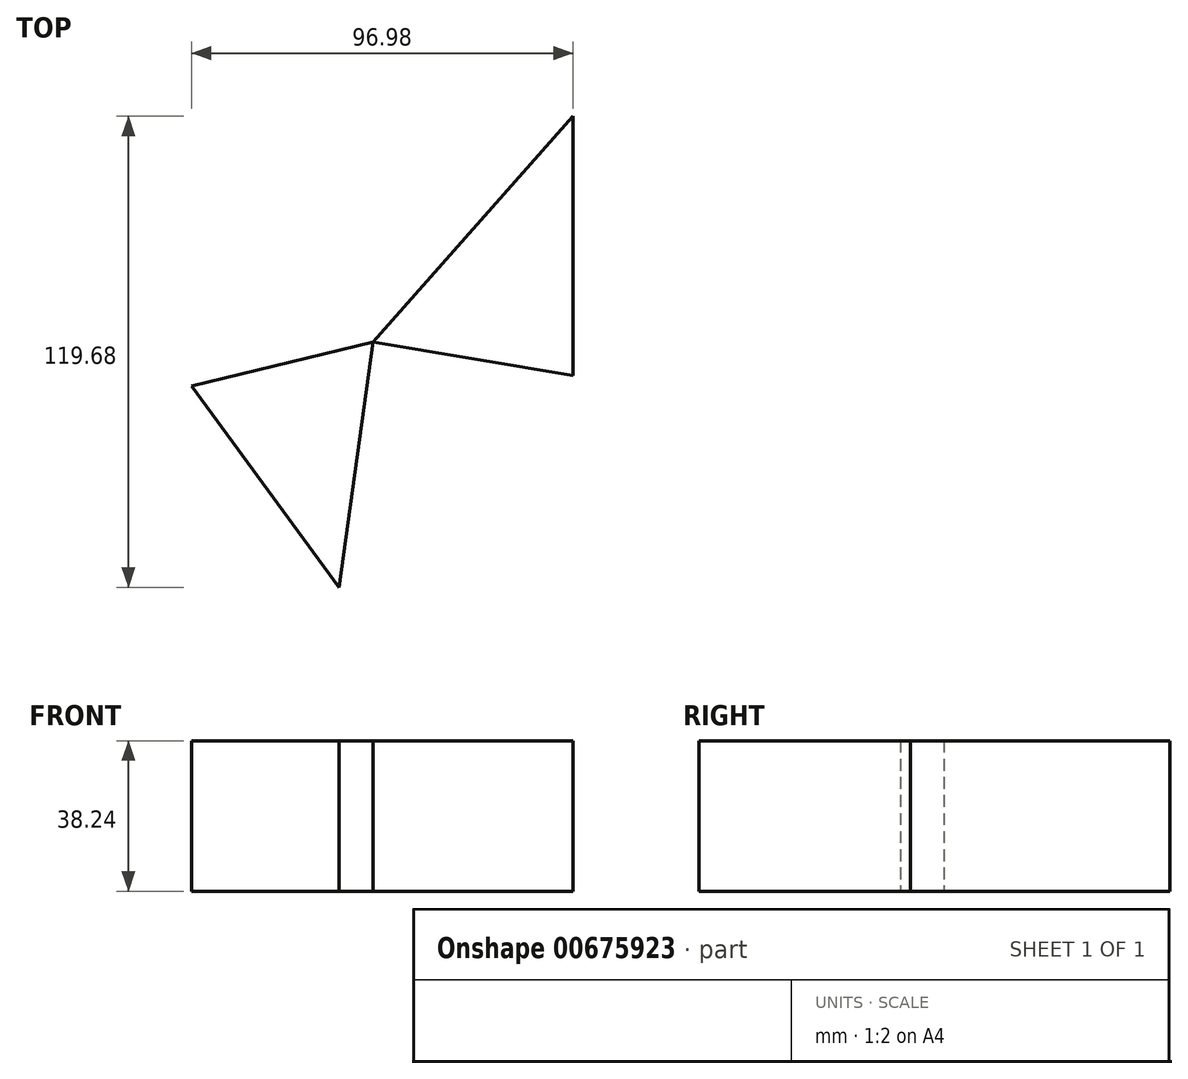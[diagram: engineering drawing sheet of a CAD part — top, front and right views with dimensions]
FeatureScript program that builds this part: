
annotation { "Feature Type Name" : "Feature", "Feature Type Description" : "" }
export const myFeature = defineFeature(function(context is Context, id is Id, definition is map)
    precondition{}
    {
        {
            var Q0;
            Q0=qCreatedBy(makeId("Top.planeOp"),FACE);
            var sketch = newSketch(context, id + "F0", { "sketchPlane" : qUnion([Q0])});
            skLineSegment(sketch, "E0", {"start": v(-46.19, 0) * mm, "end": v(0, 11.1) * mm});
            skLineSegment(sketch, "E1", {"start": v(0, 11.1) * mm, "end": v(-8.65, -51.16) * mm});
            skLineSegment(sketch, "E2", {"start": v(-8.65, -51.16) * mm, "end": v(-46.19, 0) * mm});
            skLineSegment(sketch, "E3", {"start": v(50.8, 68.52) * mm, "end": v(0, 11.1) * mm});
            skLineSegment(sketch, "E4", {"start": v(50.8, 68.52) * mm, "end": v(50.8, 2.6) * mm});
            skLineSegment(sketch, "E5", {"start": v(50.8, 2.6) * mm, "end": v(0, 11.1) * mm});
            skSolve(sketch);
        }
        {
            var Q0;
            Q0=makeQuery(id+"F0.imprint","IMPRINT",FACE,{"disambiguationData":[TD([[makeQuery(id+"F0.imprint","IMPRINT",EDGE,{"derivedFrom":sQuery(id+"F0.wireOp",EDGE,"E0")}),-1.0]])]});
            var Q1;
            Q1=makeQuery(id+"F0.imprint","IMPRINT",FACE,{"disambiguationData":[TD([[makeQuery(id+"F0.imprint","IMPRINT",EDGE,{"derivedFrom":sQuery(id+"F0.wireOp",EDGE,"E3")}),1.0]])]});
            extrude(context, id + "F1", {"entities" : qUnion([Q0, Q1]), "depth" : 38.24 * mm, "offsetDistance" : 25.4 * mm});
        }
    });
